# Revit family: 127V SENCILLA 5630 IP65_SD560.U.1_W.1_N.1
name_source: partatom
category: Luminarias
units: mm (PartAtom-declared; Revit-internal decimal feet)

## family parameters
Compartido = No
Corte con vacíos al cargar = No
Cota de conector redondo = Diámetro de uso
Origen de luz = Sí
Punto de cálculo de habitación = No
Se basa en plano de trabajo = Sí
Siempre vertical = No
Tipo de pieza = Normal

## types (3) — shared parameters
Cambio de temperatura de color de luz atenuada = <Ninguno>
Comentarios de vataje = 127V
Costo = 1 $
Fabricante = BRILLANT
Filtro de color = 16777215
Longitud de línea de emisión = 600 mm  [stored 1.9685 ft]
Longitud de símbolo de origen de luz = 1500 mm  [stored 4.92126 ft]
Lámpara = 5630 SMD
Ángulo de campo de foco = 90.00°
Ángulo de enfoque = 30.00°
Ángulo de inclinación = 60.00°
zero-valued in all types: Elevación por defecto

## per-type parameters (varying)
| type | Descripción | Modelo |
| 127V SENCILLA 5630 IP65_SD560.W.1 | TIRA LED SENCILLA DE PCB CON RECUBRIMIENTO DE PLASTICO 14MM MONOCROMATICA , CON UNA POTENCIA DE 10.26W/M DE UN TIPO DE LED 5630 SMD, USO PARA INTERIORES COMO EXTERIORES IP65, IRC80, 60 LEDS POR METRO, PRESENTACION DE 50M, TEMPERATURA EN BLANCO CALIDO 3000K, 792.91 LUMENES POR METRO, EFICIENCIA DE 77.28 LM/W, CORTE A 1M, ALIMENTADA A 127V, REQUIERE ACCESORIOS COMO CONVERTIDOR DE CORRIENTE (1 POR SEGMENTO DE TIRA), CONECTOR INTERMEDIO (CONSIDERAR EN CORTES DE TIRA O ANGULOS CERRADOS), CONECTOR AGUJA (CONSIDERAR 1PZA PRO CADA CONVERTIDOR), FUNDA TERMOCONTRACTIL (CONSIDERAR 2PZAS POR SEGMENTO DE TIRA), TAPA FINAL (CONSIDERAR 1PZA POR SEGMENTO DE TIRA) Y CLIPS DE SUJECION (CONSIDERAR 4 PZAS POR 1M) | SD560.W.1 |
| 127V SENCILLA 5630 IP65_SD560.U.1 | TIRA LED SENCILLA DE PCB CON RECUBRIMIENTO DE PLASTICO 14MM MONOCROMATICA , CON UNA POTENCIA DE 10.26W/M DE UN TIPO DE LED 5630 SMD, USO PARA INTERIORES COMO EXTERIORES IP65, IRC80, 60 LEDS POR METRO, PRESENTACION DE 50M, TEMPERATURA EN BLANCO ULTRA CALIDO 2400K, 792.91 LUMENES POR METRO, EFICIENCIA DE 77.28 LM/W, CORTE A 1M, ALIMENTADA A 127V, REQUIERE ACCESORIOS COMO CONVERTIDOR DE CORRIENTE (1 POR SEGMENTO DE TIRA), CONECTOR INTERMEDIO (CONSIDERAR EN CORTES DE TIRA O ANGULOS CERRADOS), CONECTOR AGUJA (CONSIDERAR 1PZA PRO CADA CONVERTIDOR), FUNDA TERMOCONTRACTIL (CONSIDERAR 2PZAS POR SEGMENTO DE TIRA), TAPA FINAL (CONSIDERAR 1PZA POR SEGMENTO DE TIRA) Y CLIPS DE SUJECION (CONSIDERAR 4 PZAS POR 1M) | SD560.U.1 |
| 127V SENCILLA 5630 IP65_SD560.N.1 | TIRA LED SENCILLA DE PCB CON RECUBRIMIENTO DE PLASTICO 14MM MONOCROMATICA , CON UNA POTENCIA DE 10.26W/M DE UN TIPO DE LED 5630 SMD, USO PARA INTERIORES COMO EXTERIORES IP65, IRC80, 60 LEDS POR METRO, PRESENTACION DE 50M, TEMPERATURA EN BLANCO FRIO 4500K, 792.91 LUMENES POR METRO, EFICIENCIA DE 77.28 LM/W, CORTE A 1M, ALIMENTADA A 127V, REQUIERE ACCESORIOS COMO CONVERTIDOR DE CORRIENTE (1 POR SEGMENTO DE TIRA), CONECTOR INTERMEDIO (CONSIDERAR EN CORTES DE TIRA O ANGULOS CERRADOS), CONECTOR AGUJA (CONSIDERAR 1PZA PRO CADA CONVERTIDOR), FUNDA TERMOCONTRACTIL (CONSIDERAR 2PZAS POR SEGMENTO DE TIRA), TAPA FINAL (CONSIDERAR 1PZA POR SEGMENTO DE TIRA) Y CLIPS DE SUJECION (CONSIDERAR 4 PZAS POR 1M) | SD560.N.1 |

note: [stored X ft] marks values corroborated as IEEE doubles in the binary element streams (Revit-internal decimal feet)

## geometry (parser evidence)
native form markers: Blend x2
no freeform markers — native parametric forms only
